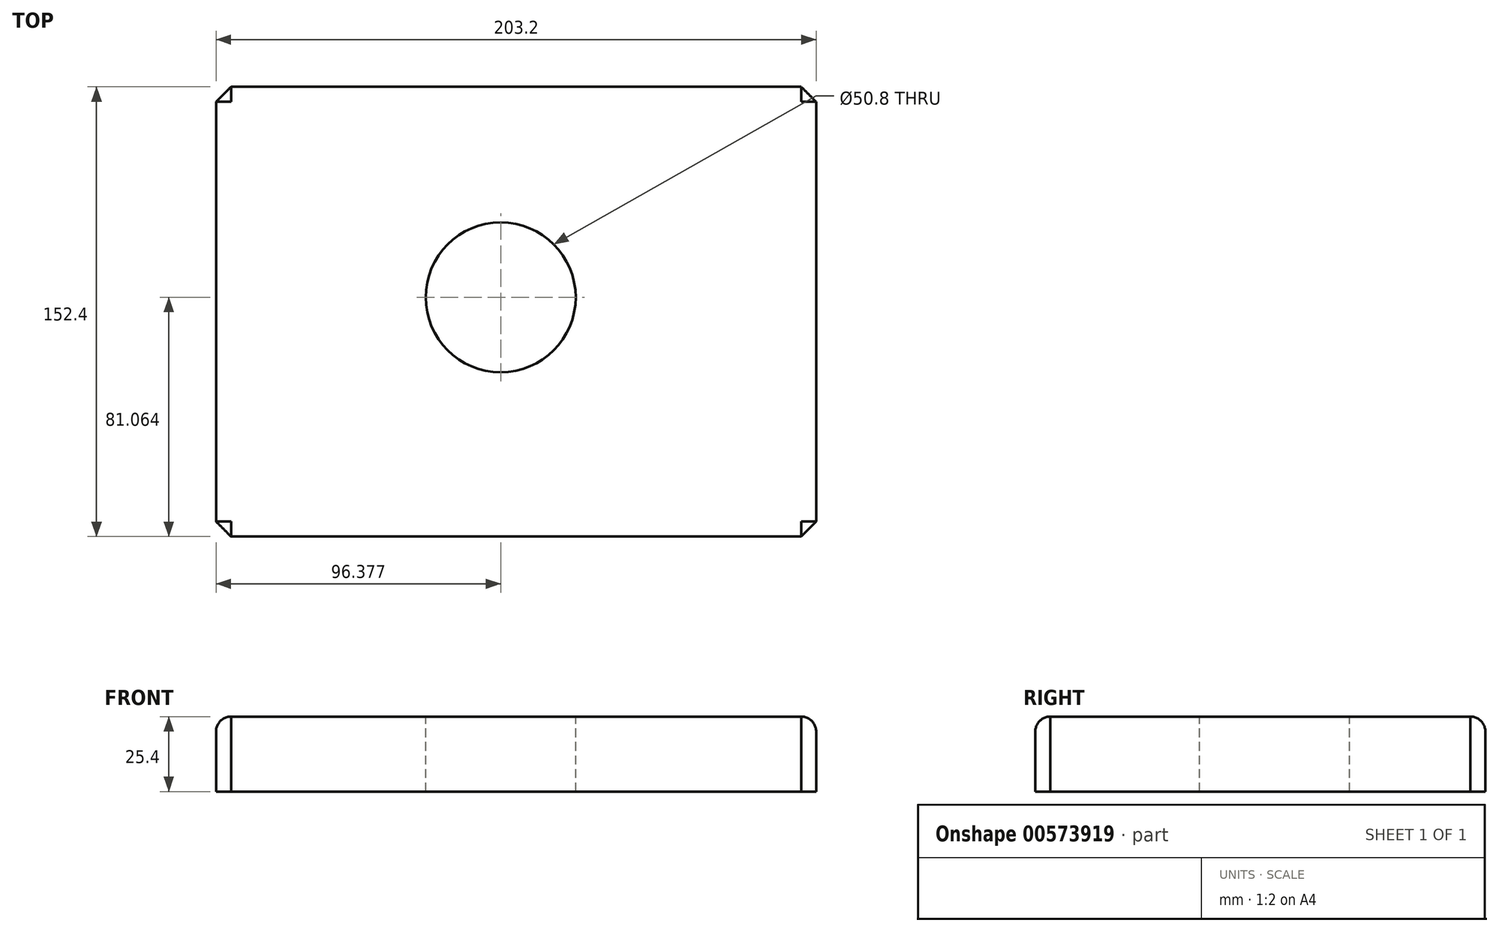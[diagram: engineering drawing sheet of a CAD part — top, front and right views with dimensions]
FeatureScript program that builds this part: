
annotation { "Feature Type Name" : "Feature", "Feature Type Description" : "" }
export const myFeature = defineFeature(function(context is Context, id is Id, definition is map)
    precondition{}
    {
        {
            var Q0;
            Q0=qCreatedBy(makeId("Top.planeOp"),FACE);
            var sketch = newSketch(context, id + "F0", { "sketchPlane" : qUnion([Q0])});
            skLineSegment(sketch, "E0.bottom", {"start": v(-46.37, -39.69) * mm, "end": v(156.83, -39.69) * mm});
            skLineSegment(sketch, "E0.top", {"start": v(-46.37, 112.71) * mm, "end": v(156.83, 112.71) * mm});
            skLineSegment(sketch, "E0.left", {"start": v(-46.37, -39.69) * mm, "end": v(-46.37, 112.71) * mm});
            skLineSegment(sketch, "E0.right", {"start": v(156.83, -39.69) * mm, "end": v(156.83, 112.71) * mm});
            skSolve(sketch);
        }
        {
            var Q0;
            Q0 = qSketchRegion(id + "F0", true);
            extrude(context, id + "F1", {"entities" : qUnion([Q0]), "depth" : 25.4 * mm, "offsetDistance" : 25.4 * mm});
        }
        {
            var Q0;
            Q0=makeQuery(id+"F1.opExtrude","CAP_FACE",FACE,{"disambiguationData":[OSD([sQuery(id+"F0.wireOp",EDGE,"E0.bottom"),sQuery(id+"F0.wireOp",EDGE,"E0.top"),sQuery(id+"F0.wireOp",EDGE,"E0.left"),sQuery(id+"F0.wireOp",EDGE,"E0.right")])],"isStart":false});
            var Q1;
            Q1=makeQuery(id+"F1.opExtrude","CAP_EDGE",EDGE,{"disambiguationData":[OSD([sQuery(id+"F0.wireOp",EDGE,"E0.bottom")])],"isStart":false});
            var Q2;
            Q2=makeQuery(id+"F1.opExtrude","CAP_EDGE",EDGE,{"disambiguationData":[OSD([sQuery(id+"F0.wireOp",EDGE,"E0.left")])],"isStart":false});
            var Q3;
            Q3=makeQuery(id+"F1.opExtrude","CAP_EDGE",EDGE,{"disambiguationData":[OSD([sQuery(id+"F0.wireOp",EDGE,"E0.top")])],"isStart":false});
            var Q4;
            Q4=makeQuery(id+"F1.opExtrude","CAP_EDGE",EDGE,{"disambiguationData":[OSD([sQuery(id+"F0.wireOp",EDGE,"E0.right")])],"isStart":false});
            fillet(context, id + "F2", {"entities" : qUnion([Q0, Q1, Q2, Q3, Q4]), "radius" : 5.08 * mm, "tangentPropagation" : true, "allowEdgeOverflow" : false});
        }
        {
            var Q0;
            Q0=makeQuery(id+"F1.opExtrude","SWEPT_EDGE",EDGE,{"disambiguationData":[OSD([sQuery(id+"F0.wireOp",EDGE,"E0.bottom"),sQuery(id+"F0.wireOp",EDGE,"E0.left")])]});
            var Q1;
            Q1=makeQuery(id+"F1.opExtrude","SWEPT_EDGE",EDGE,{"disambiguationData":[OSD([sQuery(id+"F0.wireOp",EDGE,"E0.bottom"),sQuery(id+"F0.wireOp",EDGE,"E0.right")])]});
            var Q2;
            Q2=makeQuery(id+"F1.opExtrude","SWEPT_EDGE",EDGE,{"disambiguationData":[OSD([sQuery(id+"F0.wireOp",EDGE,"E0.top"),sQuery(id+"F0.wireOp",EDGE,"E0.right")])]});
            var Q3;
            Q3=makeQuery(id+"F1.opExtrude","SWEPT_EDGE",EDGE,{"disambiguationData":[OSD([sQuery(id+"F0.wireOp",EDGE,"E0.top"),sQuery(id+"F0.wireOp",EDGE,"E0.left")])]});
            chamfer(context, id + "F3", {"entities" : qUnion([Q0, Q1, Q2, Q3]), "width" : 5.08 * mm, "tangentPropagation" : true});
        }
        {
            var Q0;
            Q0=makeQuery(id+"F1.opExtrude","CAP_FACE",FACE,{"disambiguationData":[OSD([sQuery(id+"F0.wireOp",EDGE,"E0.bottom"),sQuery(id+"F0.wireOp",EDGE,"E0.top"),sQuery(id+"F0.wireOp",EDGE,"E0.left"),sQuery(id+"F0.wireOp",EDGE,"E0.right")])],"isStart":false});
            var sketch = newSketch(context, id + "F4", { "sketchPlane" : qUnion([Q0])});
            skCircle(sketch, "E1", {"center": v(50, 41.37) * mm, "radius": 25.4 * mm});
            skSolve(sketch);
        }
        {
            var Q0;
            Q0=makeQuery(id+"F4.imprint","IMPRINT",FACE,{"disambiguationData":[TD([[makeQuery(id+"F4.imprint","IMPRINT",EDGE,{"derivedFrom":sQuery(id+"F4.wireOp",EDGE,"E1")}),1.0]])]});
            extrude(context, id + "F5", {"entities" : qUnion([Q0]), "operationType" : NewBodyOperationType.REMOVE, "oppositeDirection" : true, "depth" : 25.4 * mm, "offsetDistance" : 25.4 * mm});
        }
    });
